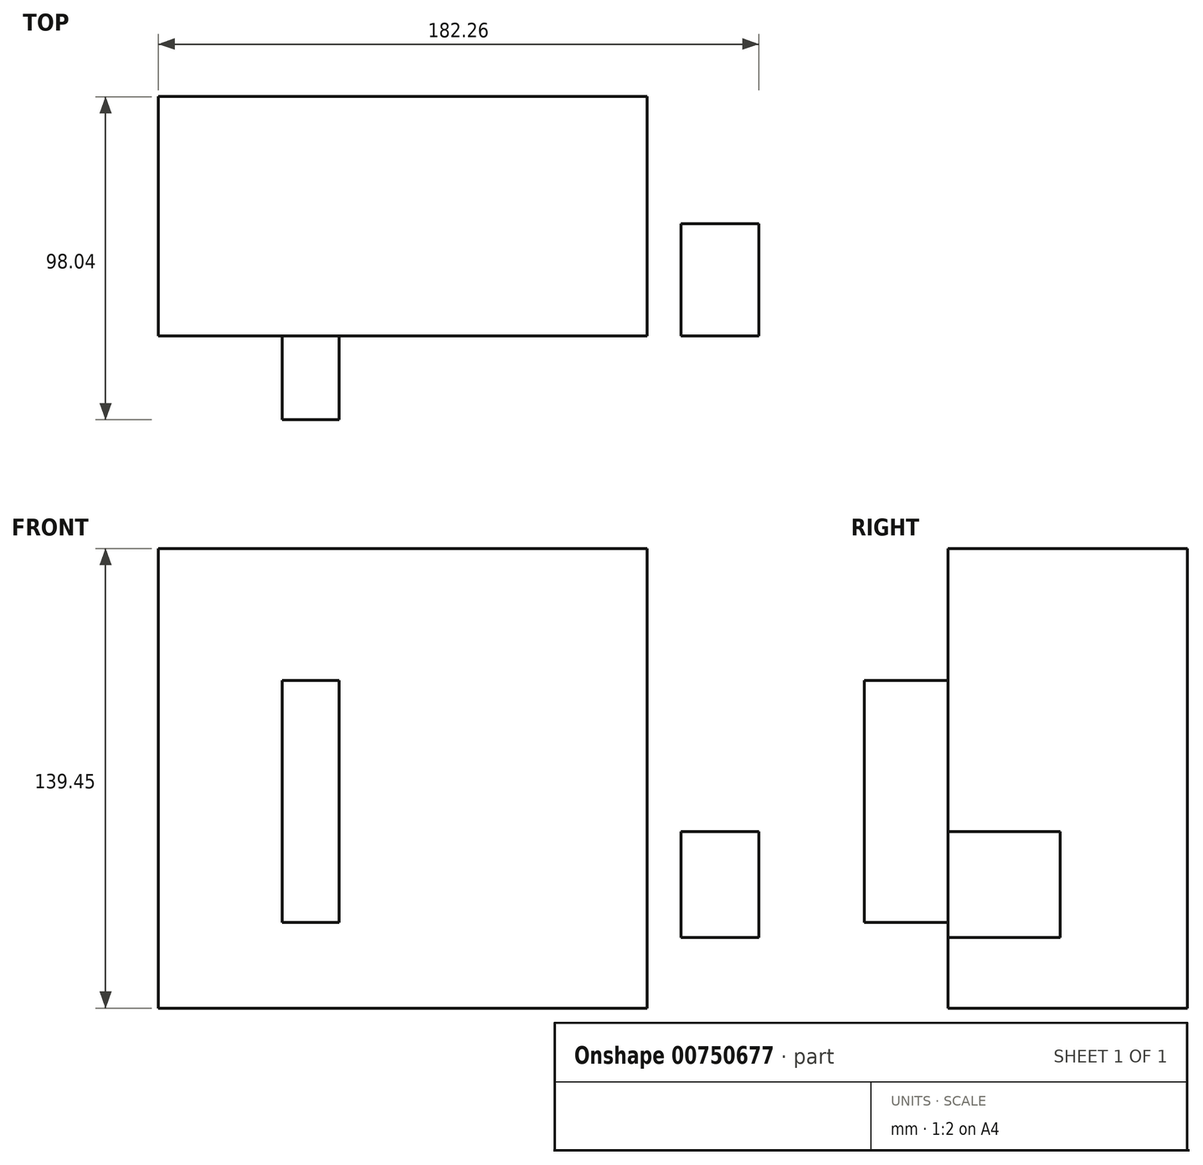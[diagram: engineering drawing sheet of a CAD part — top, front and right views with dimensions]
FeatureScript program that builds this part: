
annotation { "Feature Type Name" : "Feature", "Feature Type Description" : "" }
export const myFeature = defineFeature(function(context is Context, id is Id, definition is map)
    precondition{}
    {
        {
            var Q0;
            Q0=qCreatedBy(makeId("Front.planeOp"),FACE);
            var sketch = newSketch(context, id + "F0", { "sketchPlane" : qUnion([Q0])});
            skLineSegment(sketch, "E0.bottom", {"start": v(-75.32, -68.67) * mm, "end": v(73.04, -68.67) * mm});
            skLineSegment(sketch, "E0.top", {"start": v(-75.32, 70.78) * mm, "end": v(73.04, 70.78) * mm});
            skLineSegment(sketch, "E0.left", {"start": v(-75.32, -68.67) * mm, "end": v(-75.32, 70.78) * mm});
            skLineSegment(sketch, "E0.right", {"start": v(73.04, -68.67) * mm, "end": v(73.04, 70.78) * mm});
            skSolve(sketch);
        }
        {
            var Q0;
            Q0=makeQuery(id+"F0.imprint","IMPRINT",FACE,{"disambiguationData":[TD([[makeQuery(id+"F0.imprint","IMPRINT",EDGE,{"derivedFrom":sQuery(id+"F0.wireOp",EDGE,"E0.bottom")}),1.0]])]});
            extrude(context, id + "F1", {"entities" : qUnion([Q0]), "oppositeDirection" : true, "depth" : 72.64 * mm, "offsetDistance" : 25.4 * mm});
        }
        {
            var Q0;
            Q0=qCreatedBy(makeId("Front.planeOp"),FACE);
            var sketch = newSketch(context, id + "F2", { "sketchPlane" : qUnion([Q0])});
            skLineSegment(sketch, "E1.bottom", {"start": v(-37.7, 30.7) * mm, "end": v(-20.4, 30.7) * mm});
            skLineSegment(sketch, "E1.top", {"start": v(-37.7, -42.68) * mm, "end": v(-20.4, -42.68) * mm});
            skLineSegment(sketch, "E1.left", {"start": v(-37.7, 30.7) * mm, "end": v(-37.7, -42.68) * mm});
            skLineSegment(sketch, "E1.right", {"start": v(-20.4, 30.7) * mm, "end": v(-20.4, -42.68) * mm});
            skSolve(sketch);
        }
        {
            var Q0;
            Q0=makeQuery(id+"F2.imprint","IMPRINT",FACE,{"disambiguationData":[TD([[makeQuery(id+"F2.imprint","IMPRINT",EDGE,{"derivedFrom":sQuery(id+"F2.wireOp",EDGE,"E1.bottom")}),-1.0]])]});
            extrude(context, id + "F3", {"entities" : qUnion([Q0]), "operationType" : NewBodyOperationType.ADD, "depth" : 25.4 * mm, "offsetDistance" : 25.4 * mm});
        }
        {
            var Q0;
            Q0=qCreatedBy(makeId("Front.planeOp"),FACE);
            var sketch = newSketch(context, id + "F4", { "sketchPlane" : qUnion([Q0])});
            skLineSegment(sketch, "E2.bottom", {"start": v(83.32, -47.31) * mm, "end": v(106.94, -47.31) * mm});
            skLineSegment(sketch, "E2.top", {"start": v(83.32, -15.14) * mm, "end": v(106.94, -15.14) * mm});
            skLineSegment(sketch, "E2.left", {"start": v(83.32, -47.31) * mm, "end": v(83.32, -15.14) * mm});
            skLineSegment(sketch, "E2.right", {"start": v(106.94, -47.31) * mm, "end": v(106.94, -15.14) * mm});
            skSolve(sketch);
        }
        {
            var Q0;
            Q0=makeQuery(id+"F4.imprint","IMPRINT",FACE,{"disambiguationData":[TD([[makeQuery(id+"F4.imprint","IMPRINT",EDGE,{"derivedFrom":sQuery(id+"F4.wireOp",EDGE,"E2.bottom")}),1.0]])]});
            extrude(context, id + "F5", {"entities" : qUnion([Q0]), "oppositeDirection" : true, "depth" : 34.04 * mm, "offsetDistance" : 25.4 * mm});
        }
    });
